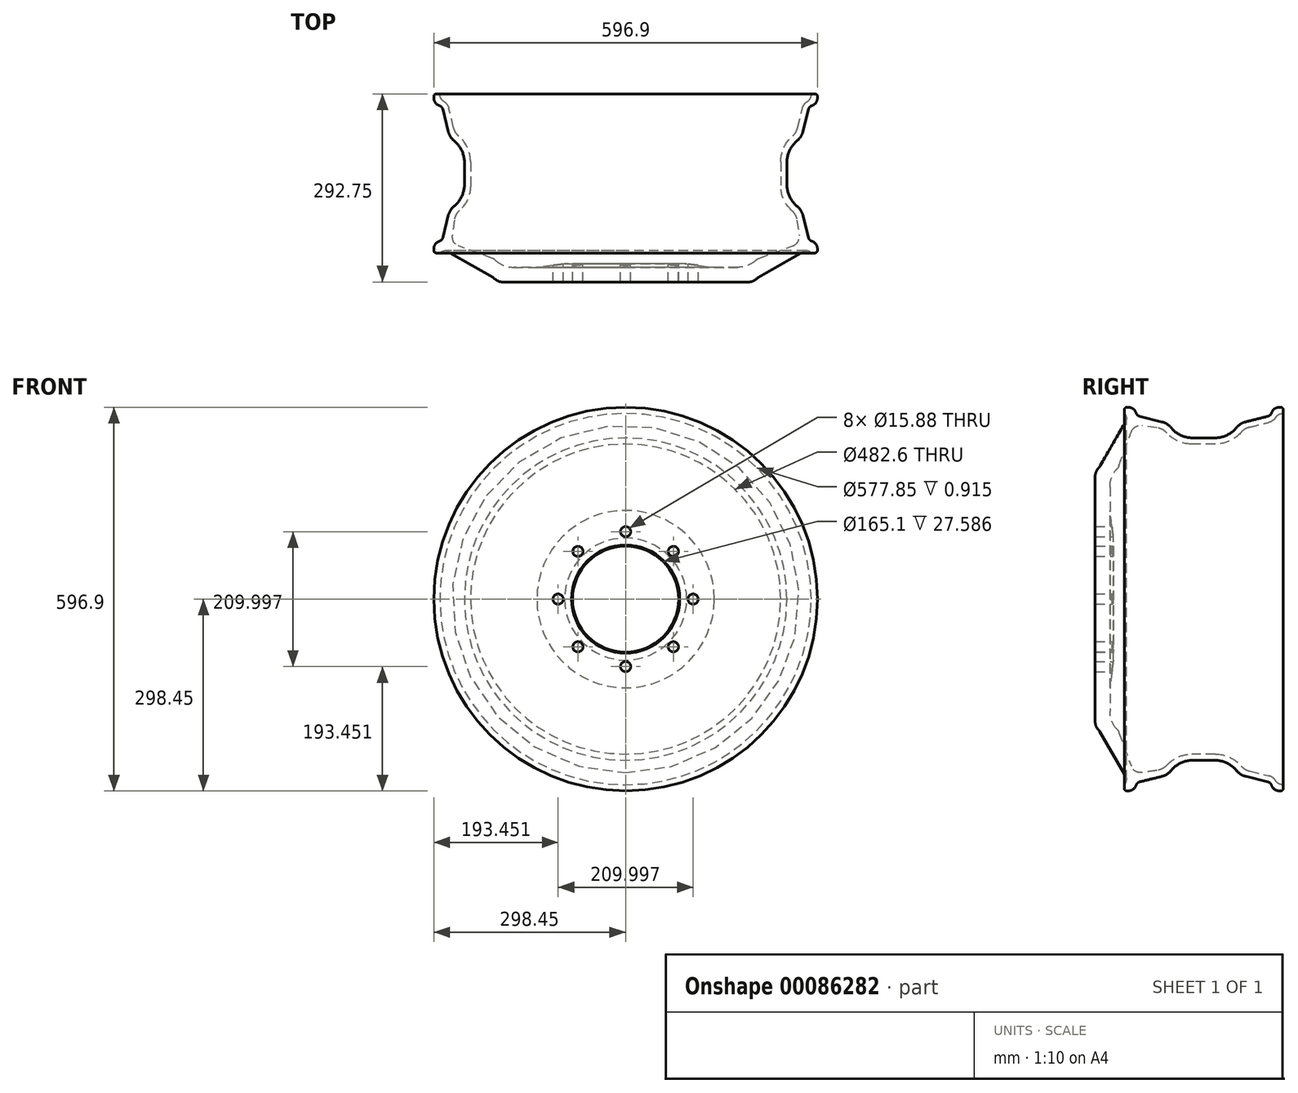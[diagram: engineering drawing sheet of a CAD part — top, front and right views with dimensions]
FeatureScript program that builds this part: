
annotation { "Feature Type Name" : "Feature", "Feature Type Description" : "" }
export const myFeature = defineFeature(function(context is Context, id is Id, definition is map)
    precondition{}
    {
        {
            var Q0;
            Q0=qCreatedBy(makeId("Right.planeOp"),FACE);
            var sketch = newSketch(context, id + "F0", { "sketchPlane" : qUnion([Q0])});
            skLineSegment(sketch, "E0", {"start": v(0, 40) * mm, "end": v(-18.76, 84.2) * mm});
            skLineSegment(sketch, "E1", {"start": v(-18.76, 84.2) * mm, "end": v(-18.76, 179.44) * mm});
            skLineSegment(sketch, "E2", {"start": v(-18.76, 198.46) * mm, "end": v(-18.76, 179.44) * mm});
            skLineSegment(sketch, "E3", {"start": v(-12.43, 205.1) * mm, "end": v(35.97, 288.93) * mm});
            skLineSegment(sketch, "E4", {"start": v(35.97, 288.93) * mm, "end": v(26.5, 288.93) * mm});
            skLineSegment(sketch, "E5", {"start": v(26.5, 288.93) * mm, "end": v(26.5, 298.45) * mm});
            skLineSegment(sketch, "E6", {"start": v(26.5, 298.45) * mm, "end": v(45.5, 298.45) * mm});
            skLineSegment(sketch, "E7", {"start": v(45.5, 298.45) * mm, "end": v(45.5, 285.75) * mm});
            skLineSegment(sketch, "E8", {"start": v(45.5, 285.75) * mm, "end": v(96.43, 273.05) * mm});
            skLineSegment(sketch, "E9", {"start": v(96.43, 273.05) * mm, "end": v(108.32, 250.83) * mm});
            skLineSegment(sketch, "E10", {"start": v(108.32, 250.83) * mm, "end": v(192.16, 250.83) * mm});
            skLineSegment(sketch, "E11", {"start": v(192.16, 250.83) * mm, "end": v(204.05, 273.05) * mm});
            skLineSegment(sketch, "E12", {"start": v(204.05, 273.05) * mm, "end": v(255, 285.75) * mm});
            skLineSegment(sketch, "E13", {"start": v(255, 285.75) * mm, "end": v(255, 298.45) * mm});
            skLineSegment(sketch, "E14", {"start": v(255, 298.45) * mm, "end": v(274, 298.45) * mm});
            skLineSegment(sketch, "E15", {"start": v(274, 298.45) * mm, "end": v(274, 288.93) * mm});
            skLineSegment(sketch, "E16", {"start": v(274, 288.93) * mm, "end": v(264.52, 288.93) * mm});
            skLineSegment(sketch, "E17", {"start": v(264.52, 288.93) * mm, "end": v(264.52, 278.3) * mm});
            skLineSegment(sketch, "E18", {"start": v(264.52, 278.3) * mm, "end": v(210.46, 264.83) * mm});
            skLineSegment(sketch, "E19", {"start": v(197.87, 241.3) * mm, "end": v(210.46, 264.83) * mm});
            skLineSegment(sketch, "E20", {"start": v(197.87, 241.3) * mm, "end": v(102.62, 241.3) * mm});
            skLineSegment(sketch, "E21", {"start": v(102.62, 241.3) * mm, "end": v(90.02, 264.83) * mm});
            skLineSegment(sketch, "E22", {"start": v(90.02, 264.83) * mm, "end": v(41.57, 271.64) * mm});
            skLineSegment(sketch, "E23", {"start": v(41.57, 271.64) * mm, "end": v(17.35, 205.1) * mm});
            skLineSegment(sketch, "E24", {"start": v(4.24, 190.73) * mm, "end": v(4.24, 138.03) * mm});
            skLineSegment(sketch, "E25", {"start": v(4.24, 138.03) * mm, "end": v(9.52, 95) * mm});
            skLineSegment(sketch, "E26", {"start": v(9.52, 95) * mm, "end": v(9.53, 40) * mm});
            skLineSegment(sketch, "E27", {"start": v(9.53, 40) * mm, "end": v(0, 40) * mm});
            skLineSegment(sketch, "E28", {"start": v(-35.45, 0) * mm, "end": v(34.97, 0) * mm, "construction": true});
            skLineSegment(sketch, "E29", {"start": v(-18.76, 198.46) * mm, "end": v(-12.43, 205.1) * mm});
            skLineSegment(sketch, "E30", {"start": v(4.24, 190.73) * mm, "end": v(17.35, 205.1) * mm});
            skSolve(sketch);
        }
        {
            var Q0;
            Q0=makeQuery(id+"F0.imprint","IMPRINT",FACE,{"disambiguationData":[TD([[makeQuery(id+"F0.imprint","IMPRINT",EDGE,{"derivedFrom":sQuery(id+"F0.wireOp",EDGE,"E0")}),-1.0]])]});
            var Q1;
            Q1=sQuery(id+"F0.wireOp",EDGE,"E28");
            revolve(context, id + "F1", {"entities" : qUnion([Q0]), "axis" : qUnion([Q1]), "revolveType" : RevolveType.FULL});
        }
        {
            var Q0;
            Q0=qCreatedBy(makeId("Front.planeOp"),FACE);
            var sketch = newSketch(context, id + "F2", { "sketchPlane" : qUnion([Q0])});
            skCircle(sketch, "E31", {"center": v(0, 0) * mm, "radius": 82.55 * mm});
            skSolve(sketch);
        }
        {
            var Q0;
            Q0=makeQuery(id+"F2.imprint","IMPRINT",FACE,{"disambiguationData":[TD([[makeQuery(id+"F2.imprint","IMPRINT",EDGE,{"derivedFrom":sQuery(id+"F2.wireOp",EDGE,"E31")}),1.0]])]});
            var Q1;
            Q1=sQuery(id+"F2.wireOp",EDGE,"E31");
            extrude(context, id + "F3", {"entities" : qUnion([Q0]), "operationType" : NewBodyOperationType.REMOVE, "surfaceEntities" : qUnion([Q1]), "endBound" : BoundingType.SYMMETRIC, "depth" : 76.2 * mm});
        }
        {
            var Q0;
            Q0=qCreatedBy(makeId("Front.planeOp"),FACE);
            var sketch = newSketch(context, id + "F4", { "sketchPlane" : qUnion([Q0])});
            skCircle(sketch, "E32", {"center": v(0, 105) * mm, "radius": 7.94 * mm});
            skCircle(sketch, "E33.1.0", {"center": v(-74.25, 74.25) * mm, "radius": 7.94 * mm});
            skCircle(sketch, "E33.2.0", {"center": v(-105, 0) * mm, "radius": 7.94 * mm});
            skPoint(sketch, "E33.center", {"position": v(0, 0) * mm});
            skCircle(sketch, "E34.1.3.0", {"center": v(-74.25, -74.25) * mm, "radius": 7.94 * mm});
            skCircle(sketch, "E34.1.4.0", {"center": v(0, -105) * mm, "radius": 7.94 * mm});
            skCircle(sketch, "E34.1.5.0", {"center": v(74.25, -74.25) * mm, "radius": 7.94 * mm});
            skCircle(sketch, "E34.1.6.0", {"center": v(105, 0) * mm, "radius": 7.94 * mm});
            skCircle(sketch, "E34.1.7.0", {"center": v(74.25, 74.25) * mm, "radius": 7.94 * mm});
            skSolve(sketch);
        }
        {
            var Q0;
            Q0=qSketchRegion(id+"F4",true);
            extrude(context, id + "F5", {"entities" : qUnion([Q0]), "operationType" : NewBodyOperationType.REMOVE, "endBound" : BoundingType.SYMMETRIC, "depth" : 76.2 * mm});
        }
        {
            var Q0;
            Q0=makeQuery(id+"F1.opRevolve","SWEPT_EDGE",EDGE,{"disambiguationData":[OSD([sQuery(id+"F0.wireOp",EDGE,"E6"),sQuery(id+"F0.wireOp",EDGE,"E7")])]});
            var Q1;
            Q1=makeQuery(id+"F1.opRevolve","SWEPT_EDGE",EDGE,{"disambiguationData":[OSD([sQuery(id+"F0.wireOp",EDGE,"E13"),sQuery(id+"F0.wireOp",EDGE,"E14")])]});
            fillet(context, id + "F6", {"entities" : qUnion([Q0, Q1]), "radius" : 12.7 * mm, "tangentPropagation" : true, "allowEdgeOverflow" : false});
        }
        {
            var Q0;
            Q0=makeQuery(id+"F6.opFillet","BLEND_EDGE",EDGE,{"blendedFrom":[makeQuery(id+"F1.opRevolve","SWEPT_EDGE",EDGE,{"disambiguationData":[OSD([sQuery(id+"F0.wireOp",EDGE,"E6"),sQuery(id+"F0.wireOp",EDGE,"E7")])]}),makeQuery(id+"F1.opRevolve","SWEPT_FACE",FACE,{"disambiguationData":[OSD([sQuery(id+"F0.wireOp",EDGE,"E8")])]})],"blendedInto":[makeQuery(id+"F1.opRevolve","SWEPT_FACE",FACE,{"disambiguationData":[OSD([sQuery(id+"F0.wireOp",EDGE,"E8")])]})]});
            var Q1;
            Q1=makeQuery(id+"F6.opFillet","BLEND_EDGE",EDGE,{"blendedFrom":[makeQuery(id+"F1.opRevolve","SWEPT_EDGE",EDGE,{"disambiguationData":[OSD([sQuery(id+"F0.wireOp",EDGE,"E13"),sQuery(id+"F0.wireOp",EDGE,"E14")])]}),makeQuery(id+"F1.opRevolve","SWEPT_FACE",FACE,{"disambiguationData":[OSD([sQuery(id+"F0.wireOp",EDGE,"E12")])]})],"blendedInto":[makeQuery(id+"F1.opRevolve","SWEPT_FACE",FACE,{"disambiguationData":[OSD([sQuery(id+"F0.wireOp",EDGE,"E12")])]})]});
            fillet(context, id + "F7", {"entities" : qUnion([Q0, Q1]), "radius" : 7.5 * mm, "tangentPropagation" : true, "allowEdgeOverflow" : false});
        }
        {
            var Q0;
            Q0=makeQuery(id+"F1.opRevolve","SWEPT_EDGE",EDGE,{"disambiguationData":[OSD([sQuery(id+"F0.wireOp",EDGE,"E5"),sQuery(id+"F0.wireOp",EDGE,"E6")])]});
            var Q1;
            Q1=makeQuery(id+"F1.opRevolve","SWEPT_EDGE",EDGE,{"disambiguationData":[OSD([sQuery(id+"F0.wireOp",EDGE,"E14"),sQuery(id+"F0.wireOp",EDGE,"E15")])]});
            fillet(context, id + "F8", {"entities" : qUnion([Q0, Q1]), "radius" : 4 * mm, "tangentPropagation" : true, "allowEdgeOverflow" : false});
        }
        {
            var Q0;
            Q0=makeQuery(id+"F1.opRevolve","SWEPT_EDGE",EDGE,{"disambiguationData":[OSD([sQuery(id+"F0.wireOp",EDGE,"E8"),sQuery(id+"F0.wireOp",EDGE,"E9")])]});
            var Q1;
            Q1=makeQuery(id+"F1.opRevolve","SWEPT_EDGE",EDGE,{"disambiguationData":[OSD([sQuery(id+"F0.wireOp",EDGE,"E11"),sQuery(id+"F0.wireOp",EDGE,"E12")])]});
            fillet(context, id + "F9", {"entities" : qUnion([Q0, Q1]), "radius" : 26.1 * mm, "tangentPropagation" : true, "allowEdgeOverflow" : false});
        }
        {
            var Q0;
            Q0=makeQuery(id+"F1.opRevolve","SWEPT_EDGE",EDGE,{"disambiguationData":[OSD([sQuery(id+"F0.wireOp",EDGE,"E9"),sQuery(id+"F0.wireOp",EDGE,"E10")])]});
            var Q1;
            Q1=makeQuery(id+"F1.opRevolve","SWEPT_EDGE",EDGE,{"disambiguationData":[OSD([sQuery(id+"F0.wireOp",EDGE,"E10"),sQuery(id+"F0.wireOp",EDGE,"E11")])]});
            fillet(context, id + "F10", {"entities" : qUnion([Q0, Q1]), "radius" : 44.45 * mm, "tangentPropagation" : true, "allowEdgeOverflow" : false});
        }
        {
            var Q0;
            Q0=makeQuery(id+"F1.opRevolve","SWEPT_EDGE",EDGE,{"disambiguationData":[OSD([sQuery(id+"F0.wireOp",EDGE,"E3"),sQuery(id+"F0.wireOp",EDGE,"E4")])]});
            fillet(context, id + "F11", {"entities" : qUnion([Q0]), "radius" : 10.4 * mm, "tangentPropagation" : true, "allowEdgeOverflow" : false});
        }
        {
            var Q0;
            Q0=makeQuery(id+"F1.opRevolve","SWEPT_EDGE",EDGE,{"disambiguationData":[OSD([sQuery(id+"F0.wireOp",EDGE,"E22"),sQuery(id+"F0.wireOp",EDGE,"E23")])]});
            fillet(context, id + "F12", {"entities" : qUnion([Q0]), "radius" : 15.2 * mm, "tangentPropagation" : true, "allowEdgeOverflow" : false});
        }
        {
            var Q0;
            Q0=makeQuery(id+"F1.opRevolve","SWEPT_EDGE",EDGE,{"disambiguationData":[OSD([sQuery(id+"F0.wireOp",EDGE,"E21"),sQuery(id+"F0.wireOp",EDGE,"E22")])]});
            var Q1;
            Q1=makeQuery(id+"F1.opRevolve","SWEPT_EDGE",EDGE,{"disambiguationData":[OSD([sQuery(id+"F0.wireOp",EDGE,"E18"),sQuery(id+"F0.wireOp",EDGE,"E19")])]});
            fillet(context, id + "F13", {"entities" : qUnion([Q0, Q1]), "radius" : 24.4 * mm, "tangentPropagation" : true, "allowEdgeOverflow" : false});
        }
        {
            var Q0;
            Q0=makeQuery(id+"F1.opRevolve","SWEPT_EDGE",EDGE,{"disambiguationData":[OSD([sQuery(id+"F0.wireOp",EDGE,"E20"),sQuery(id+"F0.wireOp",EDGE,"E21")])]});
            var Q1;
            Q1=makeQuery(id+"F1.opRevolve","SWEPT_EDGE",EDGE,{"disambiguationData":[OSD([sQuery(id+"F0.wireOp",EDGE,"E19"),sQuery(id+"F0.wireOp",EDGE,"E20")])]});
            fillet(context, id + "F14", {"entities" : qUnion([Q0, Q1]), "radius" : 52.53 * mm, "tangentPropagation" : true, "allowEdgeOverflow" : false});
        }
        {
            var Q0;
            Q0=makeQuery(id+"F1.opRevolve","SWEPT_EDGE",EDGE,{"disambiguationData":[OSD([sQuery(id+"F0.wireOp",EDGE,"E17"),sQuery(id+"F0.wireOp",EDGE,"E18")])]});
            fillet(context, id + "F15", {"entities" : qUnion([Q0]), "radius" : 17.2 * mm, "tangentPropagation" : true, "allowEdgeOverflow" : false});
        }
        {
            var Q0;
            Q0=makeQuery(id+"F15.opFillet","BLEND_EDGE",EDGE,{"blendedFrom":[makeQuery(id+"F1.opRevolve","SWEPT_EDGE",EDGE,{"disambiguationData":[OSD([sQuery(id+"F0.wireOp",EDGE,"E17"),sQuery(id+"F0.wireOp",EDGE,"E18")])]}),makeQuery(id+"F1.opRevolve","SWEPT_FACE",FACE,{"disambiguationData":[OSD([sQuery(id+"F0.wireOp",EDGE,"E16")])]})],"blendedInto":[makeQuery(id+"F1.opRevolve","SWEPT_FACE",FACE,{"disambiguationData":[OSD([sQuery(id+"F0.wireOp",EDGE,"E16")])]})]});
            fillet(context, id + "F16", {"entities" : qUnion([Q0]), "radius" : 12.7 * mm, "tangentPropagation" : true, "allowEdgeOverflow" : false});
        }
        {
            var Q0;
            {var subQ0=makeQuery(id+"F1.opRevolve","SWEPT_FACE",FACE,{"disambiguationData":[OSD([sQuery(id+"F0.wireOp",EDGE,"E16")])]});Q0=makeQuery(id+"F16.opFillet","BLEND_EDGE",EDGE,{"blendedFrom":[makeQuery(id+"F15.opFillet","BLEND_EDGE",EDGE,{"blendedFrom":[makeQuery(id+"F1.opRevolve","SWEPT_EDGE",EDGE,{"disambiguationData":[OSD([sQuery(id+"F0.wireOp",EDGE,"E17"),sQuery(id+"F0.wireOp",EDGE,"E18")])]}),subQ0],"blendedInto":[subQ0]}),subQ0],"blendedInto":[subQ0]});}
            var Q1;
            Q1=makeQuery(id+"F11.opFillet","BLEND_EDGE",EDGE,{"blendedFrom":[makeQuery(id+"F1.opRevolve","SWEPT_EDGE",EDGE,{"disambiguationData":[OSD([sQuery(id+"F0.wireOp",EDGE,"E3"),sQuery(id+"F0.wireOp",EDGE,"E4")])]}),makeQuery(id+"F1.opRevolve","SWEPT_FACE",FACE,{"disambiguationData":[OSD([sQuery(id+"F0.wireOp",EDGE,"E5")])]})],"blendedInto":[makeQuery(id+"F1.opRevolve","SWEPT_FACE",FACE,{"disambiguationData":[OSD([sQuery(id+"F0.wireOp",EDGE,"E5")])]})]});
            fillet(context, id + "F17", {"entities" : qUnion([Q0, Q1]), "radius" : 1.5 * mm, "tangentPropagation" : true, "allowEdgeOverflow" : false});
        }
        {
            var Q0;
            Q0=makeQuery(id+"F1.opRevolve","SWEPT_EDGE",EDGE,{"disambiguationData":[OSD([sQuery(id+"F0.wireOp",EDGE,"E24"),sQuery(id+"F0.wireOp",EDGE,"E30")])]});
            fillet(context, id + "F18", {"entities" : qUnion([Q0]), "radius" : 41.27 * mm, "tangentPropagation" : true, "allowEdgeOverflow" : false});
        }
        {
            var Q0;
            Q0=makeQuery(id+"F1.opRevolve","SWEPT_EDGE",EDGE,{"disambiguationData":[OSD([sQuery(id+"F0.wireOp",EDGE,"E23"),sQuery(id+"F0.wireOp",EDGE,"E30")])]});
            fillet(context, id + "F19", {"entities" : qUnion([Q0]), "radius" : 12.7 * mm, "tangentPropagation" : true, "allowEdgeOverflow" : false});
        }
        {
            var Q0;
            Q0=makeQuery(id+"F1.opRevolve","SWEPT_EDGE",EDGE,{"disambiguationData":[OSD([sQuery(id+"F0.wireOp",EDGE,"E2"),sQuery(id+"F0.wireOp",EDGE,"E29")])]});
            fillet(context, id + "F20", {"entities" : qUnion([Q0]), "radius" : 19.05 * mm, "tangentPropagation" : true, "allowEdgeOverflow" : false});
        }
        {
            var Q0;
            Q0=makeQuery(id+"F1.opRevolve","SWEPT_EDGE",EDGE,{"disambiguationData":[OSD([sQuery(id+"F0.wireOp",EDGE,"E3"),sQuery(id+"F0.wireOp",EDGE,"E29")])]});
            fillet(context, id + "F21", {"entities" : qUnion([Q0]), "radius" : 5.08 * mm, "tangentPropagation" : true, "allowEdgeOverflow" : false});
        }
    });
